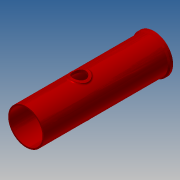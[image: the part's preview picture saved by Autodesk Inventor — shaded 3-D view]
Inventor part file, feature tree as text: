
AUTODESK INVENTOR PART (.ipt)
format: ipt  version: 2017.3 (Build 213257000, 257)  size: 317,952 bytes
history: native  units: in
note: dims shown in document units (in); Inventor stores cm internally (conversion verified against a paired STEP export)
features: other x3, extrude x3, sketch x3, pattern_circular x1, chamfer x1, projected_geometry x1
ambient origin geometry x8: Origin, YZ Plane, XZ Plane, XY Plane, X Axis, Y Axis, Z Axis, Center Point
bodies: Solid1 (feature_tree)
feature tree (12):
  other  "A1-19027-400-07 HCWI liner - trunk.ipt"
  extrude  "Extrusion1"  Depth=0.5in TaperAngle=0.0deg
  extrude  "Extrusion2"  Depth=0.5in TaperAngle=0.0deg
  extrude  "Extrusion3"  Depth=0.25in
  pattern_circular  "Circular Pattern1"  Angle=45.0deg  [1 undecoded]
  chamfer  "Chamfer1"  [1 undecoded]
  other  "Solid1::A1-19027-400-07 HCWI liner - trunk.ipt"
  other  "TaggingFeature1"
  sketch  "Sketch2"  dims[d0=0.3937in d1=0.5in d2=2.0in d3=0.0in d4=0.0in]
  sketch  "Sketch3"  dims[d5=0.5in d6=0.5in d7=0.0in d8=0.0in d9=0.5in d10=0.0in]
  sketch  "Sketch4"  dims[d11=0.7874in d12=360.0deg d14=0.25in d15=0.25in d16=0.125in d17=45.0deg]
  projected_geometry  "Projected Loop1"
note: 2 required parameter values undecoded (feature->parameter linkage not recoverable at this tier; creation-order binding heuristic only, values carry confidence <= 0.55)
